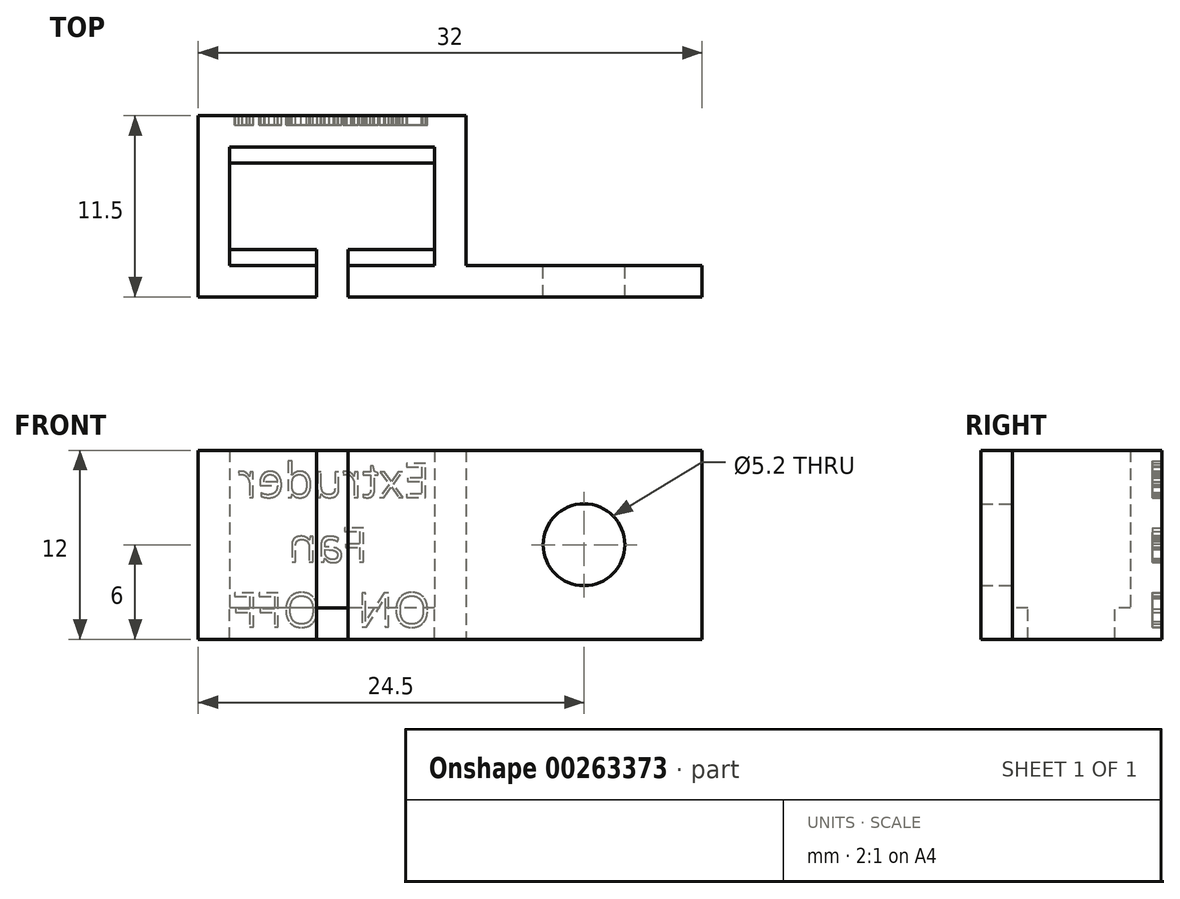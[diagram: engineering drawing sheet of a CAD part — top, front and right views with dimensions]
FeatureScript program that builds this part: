
annotation { "Feature Type Name" : "Feature", "Feature Type Description" : "" }
export const myFeature = defineFeature(function(context is Context, id is Id, definition is map)
    precondition{}
    {
        {
            var Q0;
            Q0=qCreatedBy(makeId("Top.planeOp"),FACE);
            var sketch = newSketch(context, id + "F0", { "sketchPlane" : qUnion([Q0])});
            skLineSegment(sketch, "E0.bottom", {"start": v(6.5, 3.75) * mm, "end": v(-6.5, 3.75) * mm});
            skLineSegment(sketch, "E0.top", {"start": v(6.5, -3.75) * mm, "end": v(1, -3.75) * mm});
            skLineSegment(sketch, "E0.left", {"start": v(6.5, 3.75) * mm, "end": v(6.5, -3.75) * mm});
            skLineSegment(sketch, "E0.right", {"start": v(-6.5, 3.75) * mm, "end": v(-6.5, -3.75) * mm});
            skPoint(sketch, "E0.middle", {"position": v(0, 0) * mm});
            skLineSegment(sketch, "E1.bottom", {"start": v(8.5, 5.75) * mm, "end": v(-8.5, 5.75) * mm});
            skLineSegment(sketch, "E1.top", {"start": v(8.5, -5.75) * mm, "end": v(1, -5.75) * mm});
            skLineSegment(sketch, "E1.left", {"start": v(8.5, 5.75) * mm, "end": v(8.5, -5.75) * mm});
            skLineSegment(sketch, "E1.right", {"start": v(-8.5, 5.75) * mm, "end": v(-8.5, -5.75) * mm});
            skLineSegment(sketch, "E2", {"start": v(-1, -3.75) * mm, "end": v(-1, -5.75) * mm});
            skLineSegment(sketch, "E3", {"start": v(1, -5.75) * mm, "end": v(1, -3.75) * mm});
            skLineSegment(sketch, "E4.trimOffspring", {"start": v(-1, -3.75) * mm, "end": v(-6.5, -3.75) * mm});
            skLineSegment(sketch, "E5.trimOffspring", {"start": v(-1, -5.75) * mm, "end": v(-8.5, -5.75) * mm});
            skSolve(sketch);
        }
        {
            var Q0;
            Q0=makeQuery(id+"F0.imprint","IMPRINT",FACE,{"disambiguationData":[TD([[makeQuery(id+"F0.imprint","IMPRINT",EDGE,{"derivedFrom":sQuery(id+"F0.wireOp",EDGE,"E0.bottom")}),-1.0]])]});
            extrude(context, id + "F1", {"entities" : qUnion([Q0]), "depth" : 10 * mm});
        }
        {
            var Q0;
            Q0=makeQuery(id+"F1.opExtrude","CAP_FACE",FACE,{"disambiguationData":[OSD([sQuery(id+"F0.wireOp",EDGE,"E0.bottom"),sQuery(id+"F0.wireOp",EDGE,"E0.top"),sQuery(id+"F0.wireOp",EDGE,"E0.left"),sQuery(id+"F0.wireOp",EDGE,"E0.right"),sQuery(id+"F0.wireOp",EDGE,"E1.bottom"),sQuery(id+"F0.wireOp",EDGE,"E1.top"),sQuery(id+"F0.wireOp",EDGE,"E1.left"),sQuery(id+"F0.wireOp",EDGE,"E1.right"),sQuery(id+"F0.wireOp",EDGE,"E2"),sQuery(id+"F0.wireOp",EDGE,"E3"),sQuery(id+"F0.wireOp",EDGE,"E4.trimOffspring"),sQuery(id+"F0.wireOp",EDGE,"E5.trimOffspring")])],"isStart":true});
            var sketch = newSketch(context, id + "F2", { "sketchPlane" : qUnion([Q0])});
            skLineSegment(sketch, "E6.bottom", {"start": v(-8.5, 5.75) * mm, "end": v(-1, 5.75) * mm});
            skLineSegment(sketch, "E6.top", {"start": v(-8.5, -5.75) * mm, "end": v(8.5, -5.75) * mm});
            skLineSegment(sketch, "E6.left", {"start": v(-8.5, 5.75) * mm, "end": v(-8.5, -5.75) * mm});
            skLineSegment(sketch, "E6.right", {"start": v(8.5, 5.75) * mm, "end": v(8.5, -5.75) * mm});
            skLineSegment(sketch, "E7.bottom", {"start": v(-6.5, -2.75) * mm, "end": v(6.5, -2.75) * mm});
            skLineSegment(sketch, "E7.top", {"start": v(-6.5, 2.75) * mm, "end": v(-1, 2.75) * mm});
            skLineSegment(sketch, "E7.left", {"start": v(-6.5, -2.75) * mm, "end": v(-6.5, 2.75) * mm});
            skLineSegment(sketch, "E7.right", {"start": v(6.5, -2.75) * mm, "end": v(6.5, 2.75) * mm});
            skLineSegment(sketch, "E8", {"start": v(1, 5.75) * mm, "end": v(1, 2.75) * mm});
            skLineSegment(sketch, "E9", {"start": v(-1, 5.75) * mm, "end": v(-1, 2.75) * mm});
            skLineSegment(sketch, "E10.trimOffspring", {"start": v(1, 2.75) * mm, "end": v(6.5, 2.75) * mm});
            skLineSegment(sketch, "E11.trimOffspring", {"start": v(1, 5.75) * mm, "end": v(8.5, 5.75) * mm});
            skSolve(sketch);
        }
        {
            var Q0;
            {var subQ0=sQuery(id+"F2.wireOp",EDGE,"E7.top");Q0=makeQuery(id+"F2.imprint","IMPRINT",FACE,{"disambiguationData":[TD([[makeQuery(id+"F2.imprint","IMPRINT",EDGE,{"derivedFrom":subQ0}),1.0]])]});}
            var Q1;
            {var subQ2=sQuery(id+"F2.wireOp",EDGE,"E6.bottom");Q1=makeQuery(id+"F2.imprint","IMPRINT",FACE,{"disambiguationData":[TD([[makeQuery(id+"F2.imprint","IMPRINT",EDGE,{"derivedFrom":subQ2}),1.0]])]});}
            var Q2;
            {var subQ2=sQuery(id+"F2.wireOp",EDGE,"E10.trimOffspring");Q2=makeQuery(id+"F2.imprint","IMPRINT",FACE,{"disambiguationData":[TD([[makeQuery(id+"F2.imprint","IMPRINT",EDGE,{"derivedFrom":subQ2}),1.0]])]});}
            var Q3;
            {var subQ0=sQuery(id+"F2.wireOp",EDGE,"E7.bottom");Q3=makeQuery(id+"F2.imprint","IMPRINT",FACE,{"disambiguationData":[TD([[makeQuery(id+"F2.imprint","IMPRINT",EDGE,{"derivedFrom":subQ0}),-1.0]])]});}
            extrude(context, id + "F3", {"entities" : qUnion([Q0, Q1, Q2, Q3]), "operationType" : NewBodyOperationType.ADD, "depth" : 2 * mm});
        }
        {
            var Q0;
            Q0=makeQuery(id+"F3.boolean.opBoolean","MERGE",FACE,{"derivedFrom":[makeQuery(id+"F1.opExtrude","SWEPT_FACE",FACE,{"disambiguationData":[OSD([sQuery(id+"F0.wireOp",EDGE,"E1.bottom")])]}),makeQuery(id+"F3.opExtrude","SWEPT_FACE",FACE,{"disambiguationData":[OSD([sQuery(id+"F2.wireOp",EDGE,"E6.top")])]})]});
            var sketch = newSketch(context, id + "F4", { "sketchPlane" : qUnion([Q0])});
            skText(sketch, "E12", { "text": "Extruder \n     Fan\nON   OFF", "fontName": "OpenSans-Regular.ttf"});
            const initialGuessF4  = {"E12": [-0.00624, 0.00701, 1, 0, 0.00218]};
            skSetInitialGuess(sketch, initialGuessF4);
            skSolve(sketch);
        }
        {
            var Q0;
            Q0 = qSketchRegion(id + "F4", true);
            extrude(context, id + "F5", {"entities" : qUnion([Q0]), "operationType" : NewBodyOperationType.REMOVE, "oppositeDirection" : true, "depth" : .6 * mm});
        }
        {
            var Q0;
            Q0=makeQuery(id+"F3.boolean.opBoolean","MERGE",FACE,{"derivedFrom":[makeQuery(id+"F1.opExtrude","SWEPT_FACE",FACE,{"disambiguationData":[OSD([sQuery(id+"F0.wireOp",EDGE,"E1.left")])]}),makeQuery(id+"F3.opExtrude","SWEPT_FACE",FACE,{"disambiguationData":[OSD([sQuery(id+"F2.wireOp",EDGE,"E6.right")])]})]});
            var sketch = newSketch(context, id + "F6", { "sketchPlane" : qUnion([Q0])});
            skLineSegment(sketch, "E13.bottom", {"start": v(-5.75, 10) * mm, "end": v(-3.75, 10) * mm});
            skLineSegment(sketch, "E13.top", {"start": v(-5.75, -2) * mm, "end": v(-3.75, -2) * mm});
            skLineSegment(sketch, "E13.left", {"start": v(-5.75, 10) * mm, "end": v(-5.75, -2) * mm});
            skLineSegment(sketch, "E13.right", {"start": v(-3.75, 10) * mm, "end": v(-3.75, -2) * mm});
            skSolve(sketch);
        }
        {
            var Q0;
            Q0=makeQuery(id+"F6.imprint","IMPRINT",FACE,{"disambiguationData":[TD([[makeQuery(id+"F6.imprint","IMPRINT",EDGE,{"derivedFrom":sQuery(id+"F6.wireOp",EDGE,"E13.bottom")}),1.0]])]});
            extrude(context, id + "F7", {"entities" : qUnion([Q0]), "operationType" : NewBodyOperationType.ADD, "depth" : 15 * mm});
        }
        {
            var Q0;
            Q0=makeQuery(id+"F7.opExtrude","SWEPT_FACE",FACE,{"disambiguationData":[OSD([sQuery(id+"F6.wireOp",EDGE,"E13.right")])]});
            var sketch = newSketch(context, id + "F8", { "sketchPlane" : qUnion([Q0])});
            skCircle(sketch, "E14", {"center": v(-16, 4) * mm, "radius": 2.6 * mm});
            skSolve(sketch);
        }
        {
            var Q0;
            Q0=makeQuery(id+"F8.imprint","IMPRINT",FACE,{"disambiguationData":[TD([[makeQuery(id+"F8.imprint","IMPRINT",EDGE,{"derivedFrom":sQuery(id+"F8.wireOp",EDGE,"E14")}),1.0]])]});
            extrude(context, id + "F9", {"entities" : qUnion([Q0]), "operationType" : NewBodyOperationType.REMOVE, "endBound" : BoundingType.THROUGH_ALL, "oppositeDirection" : true, "depth" : 25 * mm});
        }
    });
